# Revit family: Haworth_Massimosistema_Pillow
name_source: partatom
category: Furniture
revit_build: Autodesk Revit 2018 (Build: 20170223_1515(x64)
units: mm (PartAtom-declared; Revit-internal decimal feet)

## family parameters
Always vertical = No
Cut with Voids When Loaded = No
OmniClass Number = 23.40.20.00
OmniClass Title = General Furniture and Specialties
Room Calculation Point = No
Shared = No
Work Plane-Based = No

## types (2) — shared parameters
Actual Height = 16 1/2"
Assembly Code = E2020200
Cushion Bottom = 16 1/2"
Manufacturer = Haworth
Model = HCPF-MSC
Revision = 1
Size = Verify Final Dim. w/ Haworth
URL = https://www.haworth.com
URL - Product = https://www.haworth.com
Warranty = https://www.haworth.com

## per-type parameters (varying)
| type | Actual Depth | Actual Width | Description | Rectangle | Square |
| HCPF-MSCR | 5 1/2" | 23 1/2" | Haworth Massimosistema - Pillow - Rectangle | Yes | No |
| HCPF-MSCS | 3 1/2" | 16 1/2" | Haworth Massimosistema - Pillow - Square | No | Yes |

## geometry (parser evidence)
native form markers: Sweep x2
no freeform markers — native parametric forms only
